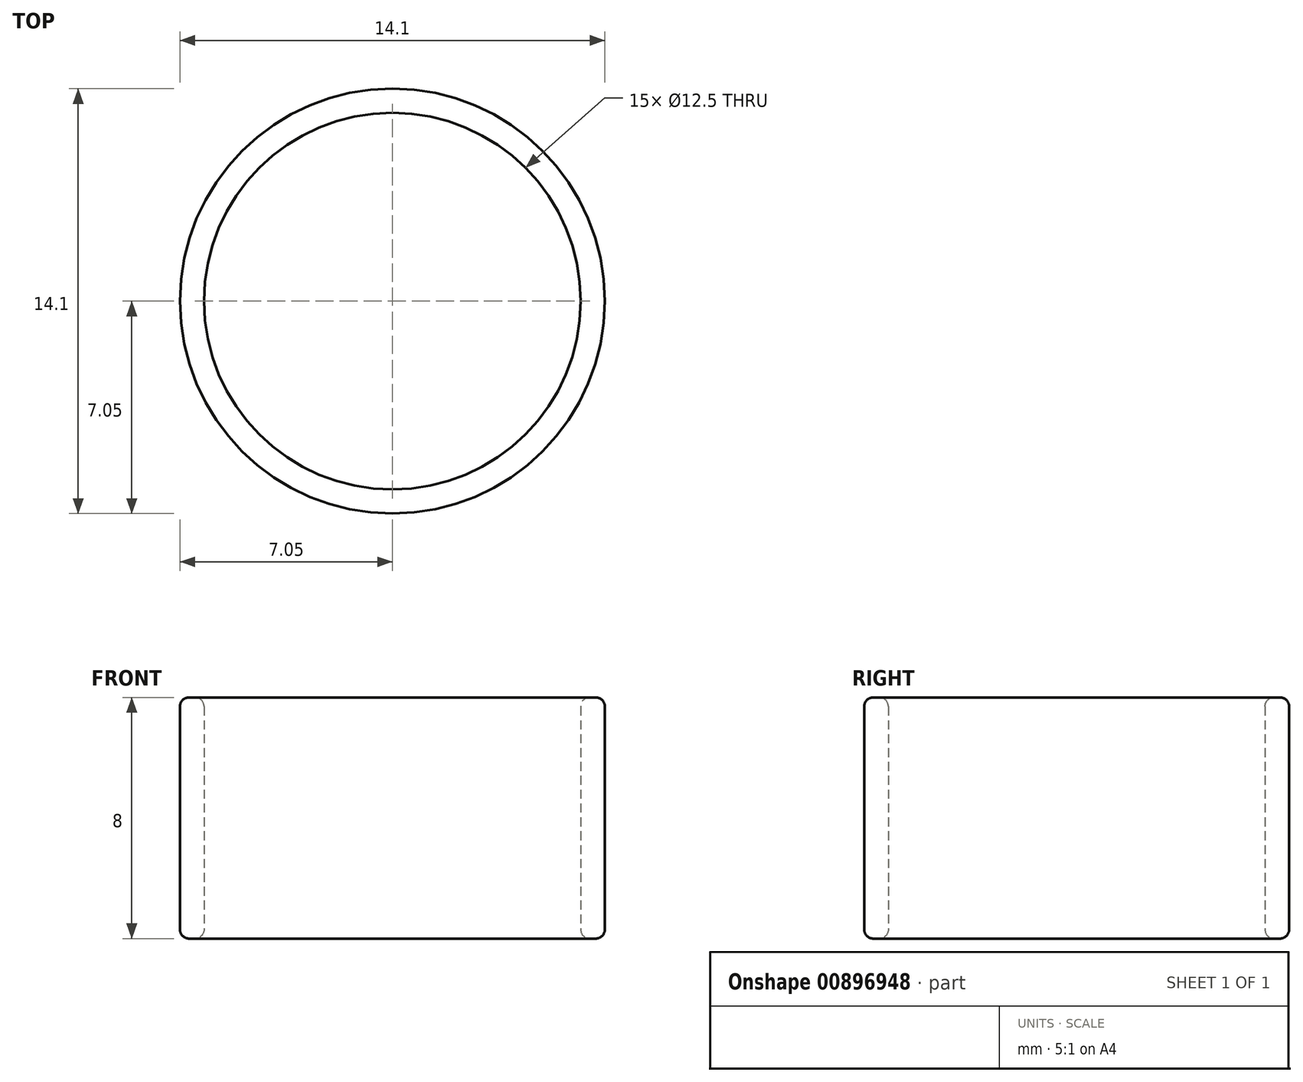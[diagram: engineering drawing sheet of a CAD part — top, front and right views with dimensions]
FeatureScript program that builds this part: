
annotation { "Feature Type Name" : "Feature", "Feature Type Description" : "" }
export const myFeature = defineFeature(function(context is Context, id is Id, definition is map)
    precondition{}
    {
        {
            var Q0;
            Q0=qCreatedBy(makeId("Top.planeOp"),FACE);
            var sketch = newSketch(context, id + "F0", { "sketchPlane" : qUnion([Q0])});
            skCircle(sketch, "E0", {"center": v(0, 0) * mm, "radius": 6.25 * mm});
            skCircle(sketch, "E1", {"center": v(0, 0) * mm, "radius": 7.05 * mm});
            skSolve(sketch);
        }
        {
            var Q0;
            Q0=makeQuery(id+"F0.imprint","IMPRINT",FACE,{"disambiguationData":[TD([[makeQuery(id+"F0.imprint","IMPRINT",EDGE,{"derivedFrom":sQuery(id+"F0.wireOp",EDGE,"E0")}),-1.0]])]});
            extrude(context, id + "F1", {"entities" : qUnion([Q0]), "depth" : 8 * mm, "offsetDistance" : 25.4 * mm});
        }
        {
            var Q0;
            Q0=makeQuery(id+"F1.opExtrude","CAP_EDGE",EDGE,{"disambiguationData":[OSD([sQuery(id+"F0.wireOp",EDGE,"E1")])],"isStart":false});
            var Q1;
            Q1=makeQuery(id+"F1.opExtrude","CAP_EDGE",EDGE,{"disambiguationData":[OSD([sQuery(id+"F0.wireOp",EDGE,"E1")])],"isStart":true});
            var Q2;
            Q2=makeQuery(id+"F1.opExtrude","SWEPT_FACE",FACE,{"disambiguationData":[OSD([sQuery(id+"F0.wireOp",EDGE,"E1")])]});
            var Q3;
            Q3=makeQuery(id+"F1.opExtrude","CAP_EDGE",EDGE,{"disambiguationData":[OSD([sQuery(id+"F0.wireOp",EDGE,"E0")])],"isStart":true});
            var Q4;
            Q4=makeQuery(id+"F1.opExtrude","CAP_EDGE",EDGE,{"disambiguationData":[OSD([sQuery(id+"F0.wireOp",EDGE,"E0")])],"isStart":false});
            fillet(context, id + "F2", {"entities" : qUnion([Q0, Q1, Q2, Q3, Q4]), "radius" : .3 * mm, "tangentPropagation" : true, "allowEdgeOverflow" : false});
        }
    });
